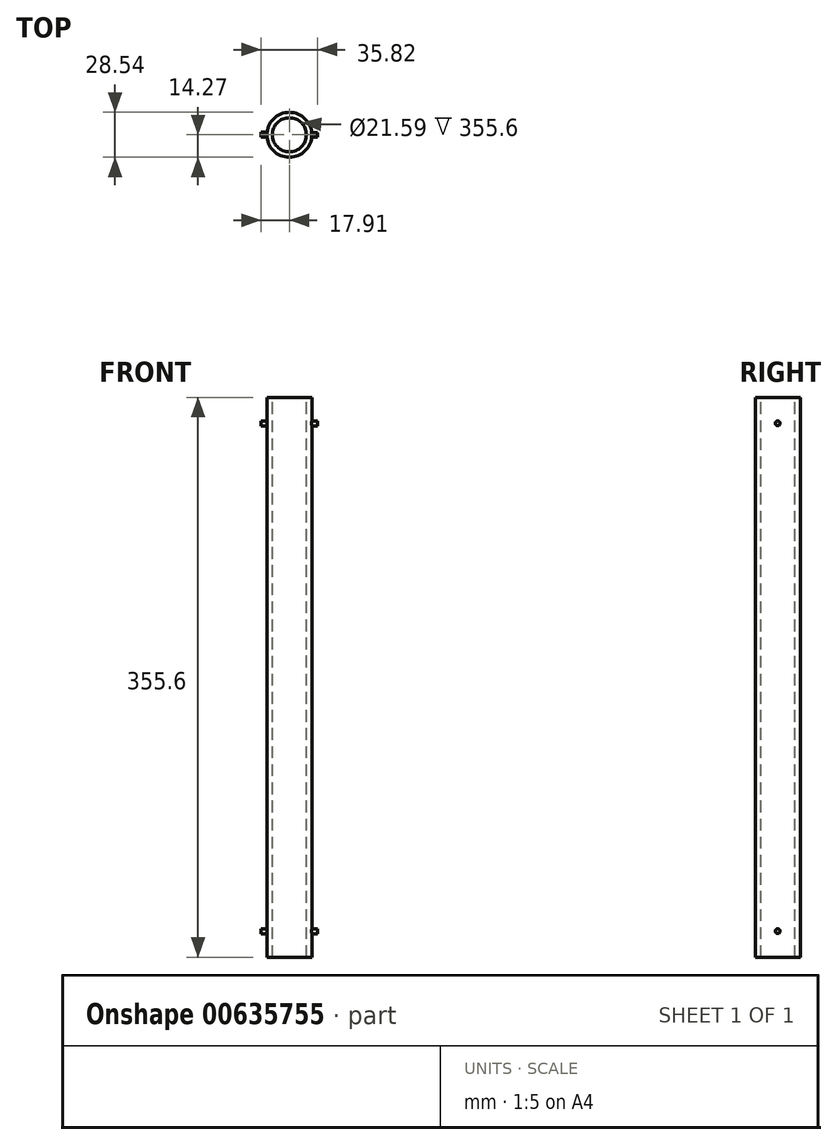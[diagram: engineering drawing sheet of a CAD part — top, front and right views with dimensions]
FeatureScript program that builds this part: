
annotation { "Feature Type Name" : "Feature", "Feature Type Description" : "" }
export const myFeature = defineFeature(function(context is Context, id is Id, definition is map)
    precondition{}
    {
        {
            var Q0;
            Q0=qCreatedBy(makeId("Top.planeOp"),FACE);
            var sketch = newSketch(context, id + "F0", { "sketchPlane" : qUnion([Q0])});
            skCircle(sketch, "E0", {"center": v(0, 0) * mm, "radius": 14.27 * mm});
            skCircle(sketch, "E1", {"center": v(0, 0) * mm, "radius": 12.83 * mm});
            skSolve(sketch);
        }
        {
            var Q0;
            Q0=qSketchRegion(id+"F0",true);
            extrude(context, id + "F1", {"entities" : qUnion([Q0]), "depth" : 266.7 * mm, "offsetDistance" : 25.4 * mm});
        }
        {
            var Q0;
            Q0=makeQuery(id+"F1.opExtrude","CAP_FACE",FACE,{"disambiguationData":[OSD([sQuery(id+"F0.wireOp",EDGE,"E0"),sQuery(id+"F0.wireOp",EDGE,"E1")])],"isStart":false});
            var sketch = newSketch(context, id + "F2", { "sketchPlane" : qUnion([Q0])});
            skArc(sketch, "E2", {"start": v(-3.17, 13.92) * mm, "mid": v(0, -14.27) * mm, "end": v(3.18, 13.92) * mm});
            skArc(sketch, "E3", {"start": v(-3.18, 12.43) * mm, "mid": v(0, -12.83) * mm, "end": v(3.18, 12.43) * mm});
            skLineSegment(sketch, "E4", {"start": v(3.18, 13.92) * mm, "end": v(3.18, 12.43) * mm});
            skLineSegment(sketch, "E5", {"start": v(-3.18, 13.92) * mm, "end": v(-3.18, 12.43) * mm});
            skSolve(sketch);
        }
        {
            var Q0;
            Q0=qSketchRegion(id+"F2",true);
            extrude(context, id + "F3", {"entities" : qUnion([Q0]), "operationType" : NewBodyOperationType.ADD, "depth" : 12.7 * mm, "offsetDistance" : 25.4 * mm});
        }
        {
            var Q0;
            Q0=makeQuery(id+"F3.opExtrude","CAP_FACE",FACE,{"disambiguationData":[OSD([sQuery(id+"F2.wireOp",EDGE,"E2"),sQuery(id+"F2.wireOp",EDGE,"E3"),sQuery(id+"F2.wireOp",EDGE,"E4"),sQuery(id+"F2.wireOp",EDGE,"E5")])],"isStart":false});
            var sketch = newSketch(context, id + "F4", { "sketchPlane" : qUnion([Q0])});
            skCircle(sketch, "E6", {"center": v(0, 0) * mm, "radius": 14.27 * mm});
            skCircle(sketch, "E7", {"center": v(0, 0) * mm, "radius": 12.83 * mm});
            skSolve(sketch);
        }
        {
            var Q0;
            Q0=qSketchRegion(id+"F4",true);
            extrude(context, id + "F5", {"entities" : qUnion([Q0]), "operationType" : NewBodyOperationType.ADD, "depth" : 76.2 * mm, "offsetDistance" : 25.4 * mm});
        }
        {
            var Q0;
            Q0=qCreatedBy(makeId("Right.planeOp"),FACE);
            cPlane(context, id + "F6", {"entities" : qUnion([Q0]), "cplaneType" : CPlaneType.OFFSET, "offset" : 12.83 * mm, "width" : 152.4 * mm, "height" : 152.4 * mm});
        }
        {
            var Q0;
            Q0=qCreatedBy(id+"F6.planeOp",FACE);
            var sketch = newSketch(context, id + "F7", { "sketchPlane" : qUnion([Q0])});
            skCircle(sketch, "E8", {"center": v(0, 12.7) * mm, "radius": 1.52 * mm});
            skSolve(sketch);
        }
        {
            var Q0;
            Q0=qSketchRegion(id+"F7",true);
            extrude(context, id + "F8", {"entities" : qUnion([Q0]), "operationType" : NewBodyOperationType.ADD, "depth" : 5.08 * mm, "offsetDistance" : 25.4 * mm});
        }
        {
            var Q0;
            Q0=qCreatedBy(makeId("Right.planeOp"),FACE);
            cPlane(context, id + "F9", {"entities" : qUnion([Q0]), "cplaneType" : CPlaneType.OFFSET, "offset" : 12.83 * mm, "oppositeDirection" : true, "width" : 152.4 * mm, "height" : 152.4 * mm});
        }
        {
            var Q0;
            Q0=qCreatedBy(id+"F9.planeOp",FACE);
            var sketch = newSketch(context, id + "F10", { "sketchPlane" : qUnion([Q0])});
            skCircle(sketch, "E9", {"center": v(0, 12.7) * mm, "radius": 1.59 * mm});
            skSolve(sketch);
        }
        {
            var Q0;
            Q0=qSketchRegion(id+"F10",true);
            extrude(context, id + "F11", {"entities" : qUnion([Q0]), "operationType" : NewBodyOperationType.ADD, "oppositeDirection" : true, "depth" : 5.08 * mm, "offsetDistance" : 25.4 * mm});
        }
        {
            var Q0;
            Q0=makeQuery(id+"F5.opExtrude","CAP_FACE",FACE,{"disambiguationData":[OSD([sQuery(id+"F4.wireOp",EDGE,"E6"),sQuery(id+"F4.wireOp",EDGE,"E7")])],"isStart":false});
            var sketch = newSketch(context, id + "F12", { "sketchPlane" : qUnion([Q0])});
            skCircle(sketch, "E10", {"center": v(0, 0) * mm, "radius": 14.29 * mm});
            skSolve(sketch);
        }
        {
            var Q0;
            Q0=qSketchRegion(id+"F12",true);
            extrude(context, id + "F13", {"entities" : qUnion([Q0]), "operationType" : NewBodyOperationType.REMOVE, "oppositeDirection" : true, "depth" : 256.54 * mm, "offsetDistance" : 25.4 * mm});
        }
        {
            var Q0;
            Q0=makeQuery(id+"F1.opExtrude","CAP_FACE",FACE,{"disambiguationData":[OSD([sQuery(id+"F0.wireOp",EDGE,"E0"),sQuery(id+"F0.wireOp",EDGE,"E1")])],"isStart":true});
            var sketch = newSketch(context, id + "F14", { "sketchPlane" : qUnion([Q0])});
            skCircle(sketch, "E11", {"center": v(0, 0) * mm, "radius": 14.27 * mm});
            skCircle(sketch, "E12", {"center": v(0, 0) * mm, "radius": 12.83 * mm});
            skSolve(sketch);
        }
        {
            var Q0;
            Q0=qSketchRegion(id+"F14",true);
            extrude(context, id + "F15", {"entities" : qUnion([Q0]), "operationType" : NewBodyOperationType.ADD, "depth" : 3.8 * mm, "offsetDistance" : 25.4 * mm});
        }
        {
            var Q0;
            Q0=makeQuery(id+"F13.boolean.opBoolean","COPY",FACE,{"derivedFrom":makeQuery(id+"F13.opExtrude","CAP_FACE",FACE,{"disambiguationData":[OSD([sQuery(id+"F12.wireOp",EDGE,"E10")])],"isStart":false})});
            var sketch = newSketch(context, id + "F16", { "sketchPlane" : qUnion([Q0])});
            skCircle(sketch, "E13", {"center": v(0, 0) * mm, "radius": 10.8 * mm});
            skCircle(sketch, "E14", {"center": v(0, 0) * mm, "radius": 14.27 * mm});
            skSolve(sketch);
        }
        {
            var Q0;
            Q0=qSketchRegion(id+"F16",true);
            extrude(context, id + "F17", {"entities" : qUnion([Q0]), "operationType" : NewBodyOperationType.ADD, "oppositeDirection" : true, "depth" : 102.87 * mm, "offsetDistance" : 25.4 * mm});
        }
        {
            var Q0;
            Q0 = qSketchRegion(id + "F16", true);
            extrude(context, id + "F18", {"entities" : qUnion([Q0]), "operationType" : NewBodyOperationType.ADD, "depth" : 74.93 * mm, "offsetDistance" : 25.4 * mm});
        }
        {
            var Q0;
            Q0=makeQuery(id+"F1.opExtrude","SWEPT_BODY",BODY,{"disambiguationData":[OSD([sQuery(id+"F0.wireOp",EDGE,"E0"),sQuery(id+"F0.wireOp",EDGE,"E1")])]});
            var Q1;
            Q1=makeQuery(id+"F18.opExtrude","CAP_FACE",FACE,{"disambiguationData":[OSD([sQuery(id+"F16.wireOp",EDGE,"E13"),sQuery(id+"F16.wireOp",EDGE,"E14")])],"isStart":false});
            mirror(context, id + "F19", {"operationType" : NewBodyOperationType.ADD, "entities" : qUnion([Q0]), "mirrorPlane" : qUnion([Q1])});
        }
    });
